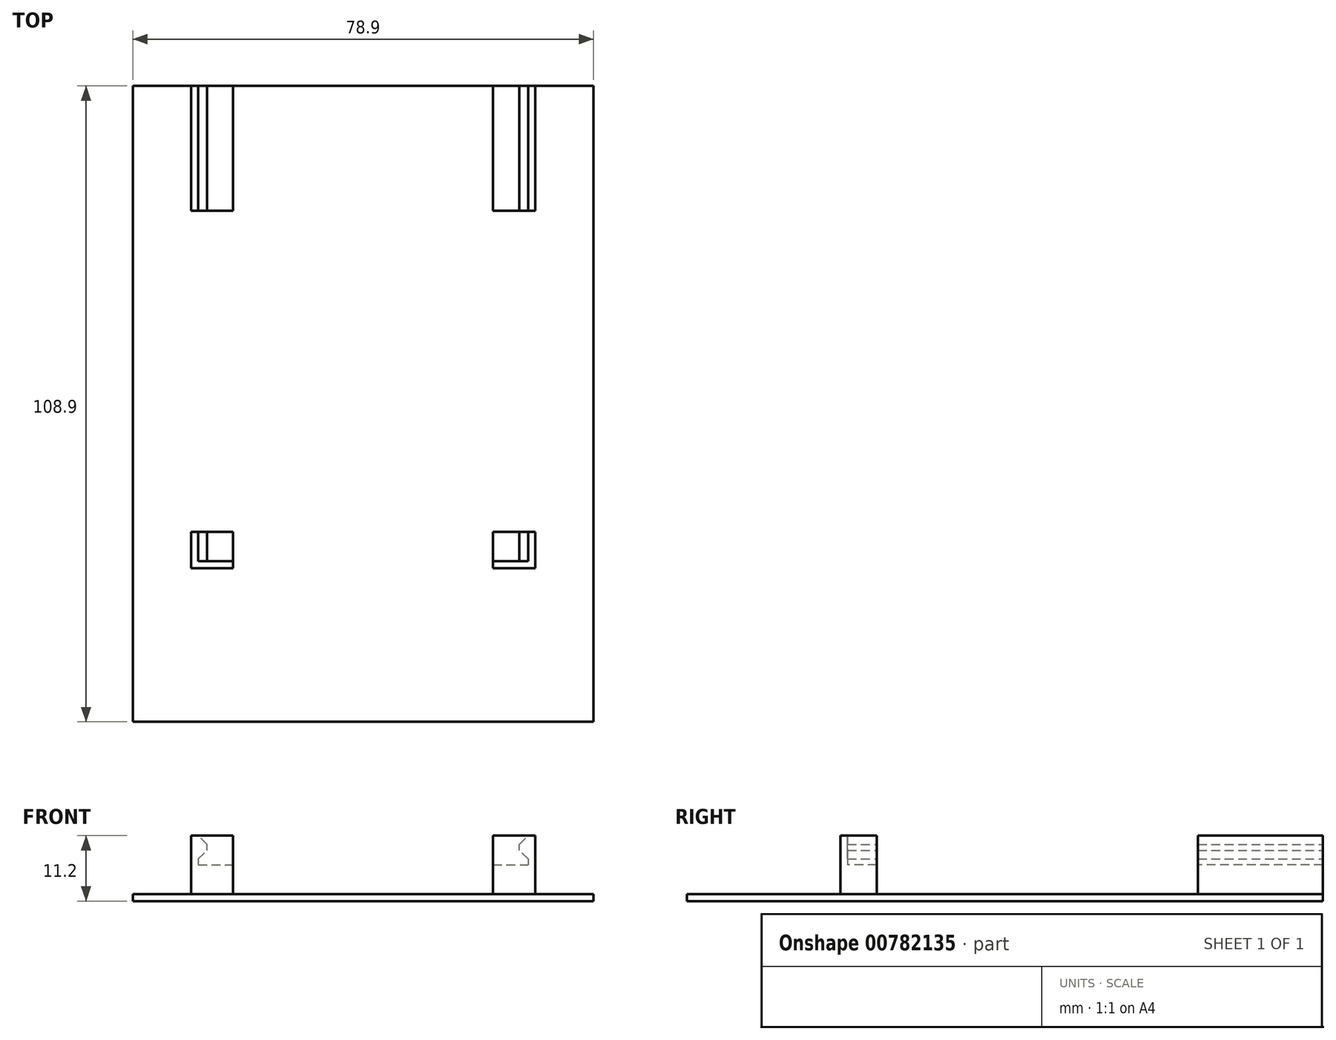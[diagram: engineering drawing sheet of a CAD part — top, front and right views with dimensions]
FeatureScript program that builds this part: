
annotation { "Feature Type Name" : "Feature", "Feature Type Description" : "" }
export const myFeature = defineFeature(function(context is Context, id is Id, definition is map)
    precondition{}
    {
        {
            var Q0;
            Q0=qCreatedBy(makeId("Top.planeOp"),FACE);
            var sketch = newSketch(context, id + "F0", { "sketchPlane" : qUnion([Q0])});
            skLineSegment(sketch, "E0.bottom", {"start": v(0, 0) * mm, "end": v(78.9, 0) * mm});
            skLineSegment(sketch, "E0.top", {"start": v(0, -76.2) * mm, "end": v(78.9, -76.2) * mm});
            skLineSegment(sketch, "E0.left", {"start": v(0, 0) * mm, "end": v(0, -76.2) * mm});
            skLineSegment(sketch, "E0.right", {"start": v(78.9, 0) * mm, "end": v(78.9, -76.2) * mm});
            skLineSegment(sketch, "E1.bottom", {"start": v(11.2, 0) * mm, "end": v(17.2, 0) * mm});
            skLineSegment(sketch, "E1.top", {"start": v(11.2, -5) * mm, "end": v(17.2, -5) * mm});
            skLineSegment(sketch, "E1.left", {"start": v(11.2, 0) * mm, "end": v(11.2, -5) * mm});
            skLineSegment(sketch, "E1.right", {"start": v(17.2, 0) * mm, "end": v(17.2, -5) * mm});
            skLineSegment(sketch, "E2.bottom", {"start": v(61.7, 0) * mm, "end": v(67.7, 0) * mm});
            skLineSegment(sketch, "E2.top", {"start": v(61.7, -5) * mm, "end": v(67.7, -5) * mm});
            skLineSegment(sketch, "E2.left", {"start": v(61.7, 0) * mm, "end": v(61.7, -5) * mm});
            skLineSegment(sketch, "E2.right", {"start": v(67.7, 0) * mm, "end": v(67.7, -5) * mm});
            skLineSegment(sketch, "E3.bottom", {"start": v(11.2, -60) * mm, "end": v(17.2, -60) * mm});
            skLineSegment(sketch, "E3.top", {"start": v(11.2, -65) * mm, "end": v(17.2, -65) * mm});
            skLineSegment(sketch, "E3.left", {"start": v(11.2, -60) * mm, "end": v(11.2, -65) * mm});
            skLineSegment(sketch, "E3.right", {"start": v(17.2, -60) * mm, "end": v(17.2, -65) * mm});
            skLineSegment(sketch, "E4.bottom", {"start": v(61.7, -60) * mm, "end": v(67.7, -60) * mm});
            skLineSegment(sketch, "E4.top", {"start": v(61.7, -65) * mm, "end": v(67.7, -65) * mm});
            skLineSegment(sketch, "E4.left", {"start": v(61.7, -60) * mm, "end": v(61.7, -65) * mm});
            skLineSegment(sketch, "E4.right", {"start": v(67.7, -60) * mm, "end": v(67.7, -65) * mm});
            skLineSegment(sketch, "E5", {"start": v(11.2, -60) * mm, "end": v(10, -60) * mm});
            skLineSegment(sketch, "E6", {"start": v(10, -60) * mm, "end": v(10, -66.2) * mm});
            skLineSegment(sketch, "E7", {"start": v(10, -66.2) * mm, "end": v(17.2, -66.2) * mm});
            skLineSegment(sketch, "E8", {"start": v(17.2, -66.2) * mm, "end": v(17.2, -65) * mm});
            skLineSegment(sketch, "E9", {"start": v(61.7, -65) * mm, "end": v(61.7, -66.2) * mm});
            skLineSegment(sketch, "E10", {"start": v(61.7, -66.2) * mm, "end": v(68.9, -66.2) * mm});
            skLineSegment(sketch, "E11", {"start": v(68.9, -66.2) * mm, "end": v(68.9, -60) * mm});
            skLineSegment(sketch, "E12", {"start": v(68.9, -60) * mm, "end": v(67.7, -60) * mm});
            skLineSegment(sketch, "E13.bottom", {"start": v(11.2, 0) * mm, "end": v(10, 0) * mm});
            skLineSegment(sketch, "E13.top", {"start": v(11.2, -5) * mm, "end": v(10, -5) * mm});
            skLineSegment(sketch, "E13.right", {"start": v(10, 0) * mm, "end": v(10, -5) * mm});
            skLineSegment(sketch, "E14.bottom", {"start": v(67.7, 0) * mm, "end": v(68.9, 0) * mm});
            skLineSegment(sketch, "E14.top", {"start": v(67.7, -5) * mm, "end": v(68.9, -5) * mm});
            skLineSegment(sketch, "E14.right", {"start": v(68.9, 0) * mm, "end": v(68.9, -5) * mm});
            skSolve(sketch);
        }
        {
            var Q0;
            Q0=makeQuery(id+"F0.imprint","IMPRINT",FACE,{"disambiguationData":[TD([[makeQuery(id+"F0.imprint","IMPRINT",EDGE,{"derivedFrom":sQuery(id+"F0.wireOp",EDGE,"E1.top")}),1.0]])]});
            var Q1;
            {var subQ0=sQuery(id+"F0.wireOp",EDGE,"E1.left");Q1=makeQuery(id+"F0.imprint","IMPRINT",FACE,{"disambiguationData":[TD([[makeQuery(id+"F0.imprint","IMPRINT",EDGE,{"derivedFrom":subQ0}),-1.0]])]});}
            var Q2;
            Q2=makeQuery(id+"F0.imprint","IMPRINT",FACE,{"disambiguationData":[TD([[makeQuery(id+"F0.imprint","IMPRINT",EDGE,{"derivedFrom":sQuery(id+"F0.wireOp",EDGE,"E0.top")}),1.0]])]});
            var Q3;
            Q3=makeQuery(id+"F0.imprint","IMPRINT",FACE,{"disambiguationData":[TD([[makeQuery(id+"F0.imprint","IMPRINT",EDGE,{"derivedFrom":sQuery(id+"F0.wireOp",EDGE,"E2.top")}),1.0]])]});
            var Q4;
            {var subQ0=sQuery(id+"F0.wireOp",EDGE,"E2.right");Q4=makeQuery(id+"F0.imprint","IMPRINT",FACE,{"disambiguationData":[TD([[makeQuery(id+"F0.imprint","IMPRINT",EDGE,{"derivedFrom":subQ0}),1.0]])]});}
            var Q5;
            Q5=makeQuery(id+"F0.imprint","IMPRINT",FACE,{"disambiguationData":[TD([[makeQuery(id+"F0.imprint","IMPRINT",EDGE,{"derivedFrom":sQuery(id+"F0.wireOp",EDGE,"E4.bottom")}),-1.0]])]});
            var Q6;
            Q6=makeQuery(id+"F0.imprint","IMPRINT",FACE,{"disambiguationData":[TD([[makeQuery(id+"F0.imprint","IMPRINT",EDGE,{"derivedFrom":sQuery(id+"F0.wireOp",EDGE,"E4.top")}),-1.0]])]});
            var Q7;
            Q7=makeQuery(id+"F0.imprint","IMPRINT",FACE,{"disambiguationData":[TD([[makeQuery(id+"F0.imprint","IMPRINT",EDGE,{"derivedFrom":sQuery(id+"F0.wireOp",EDGE,"E3.bottom")}),-1.0]])]});
            var Q8;
            Q8=makeQuery(id+"F0.imprint","IMPRINT",FACE,{"disambiguationData":[TD([[makeQuery(id+"F0.imprint","IMPRINT",EDGE,{"derivedFrom":sQuery(id+"F0.wireOp",EDGE,"E3.top")}),-1.0]])]});
            extrude(context, id + "F1", {"entities" : qUnion([Q0, Q1, Q2, Q3, Q4, Q5, Q6, Q7, Q8]), "oppositeDirection" : true, "depth" : 1.2 * mm, "offsetDistance" : 25 * mm});
        }
        {
            var Q0;
            Q0=makeQuery(id+"F0.imprint","IMPRINT",FACE,{"disambiguationData":[TD([[makeQuery(id+"F0.imprint","IMPRINT",EDGE,{"derivedFrom":sQuery(id+"F0.wireOp",EDGE,"E1.top")}),1.0]])]});
            var Q1;
            Q1=makeQuery(id+"F0.imprint","IMPRINT",FACE,{"disambiguationData":[TD([[makeQuery(id+"F0.imprint","IMPRINT",EDGE,{"derivedFrom":sQuery(id+"F0.wireOp",EDGE,"E3.bottom")}),-1.0]])]});
            var Q2;
            Q2=makeQuery(id+"F0.imprint","IMPRINT",FACE,{"disambiguationData":[TD([[makeQuery(id+"F0.imprint","IMPRINT",EDGE,{"derivedFrom":sQuery(id+"F0.wireOp",EDGE,"E2.top")}),1.0]])]});
            var Q3;
            Q3=makeQuery(id+"F0.imprint","IMPRINT",FACE,{"disambiguationData":[TD([[makeQuery(id+"F0.imprint","IMPRINT",EDGE,{"derivedFrom":sQuery(id+"F0.wireOp",EDGE,"E4.bottom")}),-1.0]])]});
            extrude(context, id + "F2", {"entities" : qUnion([Q0, Q1, Q2, Q3]), "operationType" : NewBodyOperationType.ADD, "depth" : 5 * mm, "offsetDistance" : 25 * mm});
        }
        {
            var Q0;
            Q0=makeQuery(id+"F0.imprint","IMPRINT",FACE,{"disambiguationData":[TD([[makeQuery(id+"F0.imprint","IMPRINT",EDGE,{"derivedFrom":sQuery(id+"F0.wireOp",EDGE,"E3.top")}),-1.0]])]});
            var Q1;
            Q1=makeQuery(id+"F0.imprint","IMPRINT",FACE,{"disambiguationData":[TD([[makeQuery(id+"F0.imprint","IMPRINT",EDGE,{"derivedFrom":sQuery(id+"F0.wireOp",EDGE,"E4.top")}),-1.0]])]});
            var Q2;
            {var subQ0=sQuery(id+"F0.wireOp",EDGE,"E2.right");Q2=makeQuery(id+"F0.imprint","IMPRINT",FACE,{"disambiguationData":[TD([[makeQuery(id+"F0.imprint","IMPRINT",EDGE,{"derivedFrom":subQ0}),1.0]])]});}
            var Q3;
            {var subQ0=sQuery(id+"F0.wireOp",EDGE,"E1.left");Q3=makeQuery(id+"F0.imprint","IMPRINT",FACE,{"disambiguationData":[TD([[makeQuery(id+"F0.imprint","IMPRINT",EDGE,{"derivedFrom":subQ0}),-1.0]])]});}
            extrude(context, id + "F3", {"entities" : qUnion([Q0, Q1, Q2, Q3]), "operationType" : NewBodyOperationType.ADD, "depth" : 10 * mm, "offsetDistance" : 25 * mm});
        }
        {
            var Q0;
            {var subQ0=sQuery(id+"F0.wireOp",EDGE,"E0.bottom");var subQ1=makeQuery(id+"F0.imprint","INTERSECT",VERTEX,{"derivedFrom":[subQ0,sQuery(id+"F0.wireOp",EDGE,"E1.left")]});var subQ2=makeQuery(id+"F0.imprint","INTERSECT",VERTEX,{"derivedFrom":[subQ0,sQuery(id+"F0.wireOp",EDGE,"E2.right")]});Q0=makeQuery(id+"F3.boolean.opBoolean","MERGE",FACE,{"derivedFrom":[makeQuery(id+"F2.boolean.opBoolean","MERGE",FACE,{"derivedFrom":[makeQuery(id+"F1.opExtrude","SWEPT_FACE",FACE,{"disambiguationData":[OSD([subQ0])]}),makeQuery(id+"F2.opExtrude","SWEPT_FACE",FACE,{"disambiguationData":[OSD([subQ0]),TDD([makeQuery(id+"F0.imprint","IMPRINT",EDGE,{"disambiguationData":[TD([[makeQuery(id+"F0.imprint","INTERSECT",VERTEX,{"derivedFrom":[subQ0,sQuery(id+"F0.wireOp",EDGE,"E2.left")]}),-1.0]])],"derivedFrom":subQ0})])]}),makeQuery(id+"F2.opExtrude","SWEPT_FACE",FACE,{"disambiguationData":[OSD([subQ0]),TDD([makeQuery(id+"F0.imprint","IMPRINT",EDGE,{"disambiguationData":[TD([[makeQuery(id+"F0.imprint","INTERSECT",VERTEX,{"derivedFrom":[subQ0,sQuery(id+"F0.wireOp",EDGE,"E1.right")]}),1.0]])],"derivedFrom":subQ0})])]})]}),makeQuery(id+"F3.opExtrude","SWEPT_FACE",FACE,{"disambiguationData":[OSD([subQ0]),TDD([makeQuery(id+"F0.imprint","IMPRINT",EDGE,{"disambiguationData":[TD([[subQ2,-1.0]])],"derivedFrom":subQ0})])]}),makeQuery(id+"F3.opExtrude","SWEPT_FACE",FACE,{"disambiguationData":[OSD([subQ0]),TDD([makeQuery(id+"F0.imprint","IMPRINT",EDGE,{"disambiguationData":[TD([[subQ1,1.0]])],"derivedFrom":subQ0})])]})]});}
            var sketch = newSketch(context, id + "F4", { "sketchPlane" : qUnion([Q0])});
            skLineSegment(sketch, "E15", {"start": v(-11.2, 10) * mm, "end": v(-12.7, 8.5) * mm});
            skLineSegment(sketch, "E16", {"start": v(-12.7, 8.5) * mm, "end": v(-12.7, 7.5) * mm});
            skLineSegment(sketch, "E17", {"start": v(-12.7, 7.5) * mm, "end": v(-11.2, 6) * mm});
            skLineSegment(sketch, "E18", {"start": v(-11.2, 6) * mm, "end": v(-11.2, 10) * mm});
            skLineSegment(sketch, "E19", {"start": v(-61.7, 0) * mm, "end": v(-17.2, 0) * mm, "construction": true});
            skLineSegment(sketch, "E20", {"start": v(-39.45, 0) * mm, "end": v(-39.45, 14.98) * mm, "construction": true});
            skLineSegment(sketch, "E21.MirrorCS", {"start": v(-66.2, 8.5) * mm, "end": v(-66.2, 7.5) * mm});
            skLineSegment(sketch, "E22.MirrorCS", {"start": v(-67.7, 6) * mm, "end": v(-67.7, 10) * mm});
            skLineSegment(sketch, "E23.MirrorCS", {"start": v(-67.7, 10) * mm, "end": v(-66.2, 8.5) * mm});
            skLineSegment(sketch, "E24.MirrorCS", {"start": v(-66.2, 7.5) * mm, "end": v(-67.7, 6) * mm});
            skSolve(sketch);
        }
        {
            var Q0;
            Q0=qSketchRegion(id+"F4",true);
            var Q1;
            Q1=makeQuery(id+"F3.opExtrude","SWEPT_FACE",FACE,{"disambiguationData":[OSD([sQuery(id+"F0.wireOp",EDGE,"E3.top")])]});
            extrude(context, id + "F5", {"entities" : qUnion([Q0]), "operationType" : NewBodyOperationType.ADD, "endBound" : BoundingType.UP_TO_SURFACE, "oppositeDirection" : true, "depth" : 25 * mm, "endBoundEntityFace" : qUnion([Q1]), "offsetDistance" : 25 * mm});
        }
        {
            var Q0;
            Q0=makeQuery(id+"F0.imprint","IMPRINT",FACE,{"disambiguationData":[TD([[makeQuery(id+"F0.imprint","IMPRINT",EDGE,{"derivedFrom":sQuery(id+"F0.wireOp",EDGE,"E0.top")}),1.0]])]});
            var Q1;
            Q1=makeQuery(id+"F3.opExtrude","CAP_FACE",FACE,{"disambiguationData":[OSD([sQuery(id+"F0.wireOp",EDGE,"E0.bottom"),sQuery(id+"F0.wireOp",EDGE,"E1.left"),sQuery(id+"F0.wireOp",EDGE,"E13.top"),sQuery(id+"F0.wireOp",EDGE,"E13.right")])],"isStart":false});
            extrude(context, id + "F6", {"entities" : qUnion([Q0]), "operationType" : NewBodyOperationType.REMOVE, "endBound" : BoundingType.UP_TO_SURFACE, "depth" : 19.3 * mm, "endBoundEntityFace" : qUnion([Q1]), "offsetDistance" : 25 * mm});
        }
        {
            var Q0;
            Q0=makeQuery(id+"F1.opExtrude","SWEPT_FACE",FACE,{"disambiguationData":[OSD([sQuery(id+"F0.wireOp",EDGE,"E0.top")])]});
            extrude(context, id + "F7", {"entities" : qUnion([Q0]), "operationType" : NewBodyOperationType.ADD, "depth" : 16.3 * mm, "offsetDistance" : 25 * mm});
        }
        {
            var Q0;
            {var subQ0=sQuery(id+"F0.wireOp",EDGE,"E0.bottom");var subQ1=makeQuery(id+"F0.imprint","INTERSECT",VERTEX,{"derivedFrom":[subQ0,sQuery(id+"F0.wireOp",EDGE,"E1.left")]});var subQ2=makeQuery(id+"F0.imprint","INTERSECT",VERTEX,{"derivedFrom":[subQ0,sQuery(id+"F0.wireOp",EDGE,"E2.right")]});Q0=makeQuery(id+"F5.boolean.opBoolean","MERGE",FACE,{"derivedFrom":[makeQuery(id+"F3.boolean.opBoolean","MERGE",FACE,{"derivedFrom":[makeQuery(id+"F2.boolean.opBoolean","MERGE",FACE,{"derivedFrom":[makeQuery(id+"F1.opExtrude","SWEPT_FACE",FACE,{"disambiguationData":[OSD([subQ0])]}),makeQuery(id+"F2.opExtrude","SWEPT_FACE",FACE,{"disambiguationData":[OSD([subQ0]),TDD([makeQuery(id+"F0.imprint","IMPRINT",EDGE,{"disambiguationData":[TD([[makeQuery(id+"F0.imprint","INTERSECT",VERTEX,{"derivedFrom":[subQ0,sQuery(id+"F0.wireOp",EDGE,"E2.left")]}),-1.0]])],"derivedFrom":subQ0})])]}),makeQuery(id+"F2.opExtrude","SWEPT_FACE",FACE,{"disambiguationData":[OSD([subQ0]),TDD([makeQuery(id+"F0.imprint","IMPRINT",EDGE,{"disambiguationData":[TD([[makeQuery(id+"F0.imprint","INTERSECT",VERTEX,{"derivedFrom":[subQ0,sQuery(id+"F0.wireOp",EDGE,"E1.right")]}),1.0]])],"derivedFrom":subQ0})])]})]}),makeQuery(id+"F3.opExtrude","SWEPT_FACE",FACE,{"disambiguationData":[OSD([subQ0]),TDD([makeQuery(id+"F0.imprint","IMPRINT",EDGE,{"disambiguationData":[TD([[subQ2,-1.0]])],"derivedFrom":subQ0})])]}),makeQuery(id+"F3.opExtrude","SWEPT_FACE",FACE,{"disambiguationData":[OSD([subQ0]),TDD([makeQuery(id+"F0.imprint","IMPRINT",EDGE,{"disambiguationData":[TD([[subQ1,1.0]])],"derivedFrom":subQ0})])]})]}),makeQuery(id+"F5.opExtrude","CAP_FACE",FACE,{"disambiguationData":[OSD([sQuery(id+"F4.wireOp",EDGE,"E15"),sQuery(id+"F4.wireOp",EDGE,"E16"),sQuery(id+"F4.wireOp",EDGE,"E17"),sQuery(id+"F4.wireOp",EDGE,"E18")])],"isStart":true}),makeQuery(id+"F5.opExtrude","CAP_FACE",FACE,{"disambiguationData":[OSD([sQuery(id+"F4.wireOp",EDGE,"E21.MirrorCS"),sQuery(id+"F4.wireOp",EDGE,"E22.MirrorCS"),sQuery(id+"F4.wireOp",EDGE,"E23.MirrorCS"),sQuery(id+"F4.wireOp",EDGE,"E24.MirrorCS")])],"isStart":true})]});}
            extrude(context, id + "F8", {"entities" : qUnion([Q0]), "operationType" : NewBodyOperationType.ADD, "depth" : 16.4 * mm, "offsetDistance" : 25 * mm});
        }
    });
